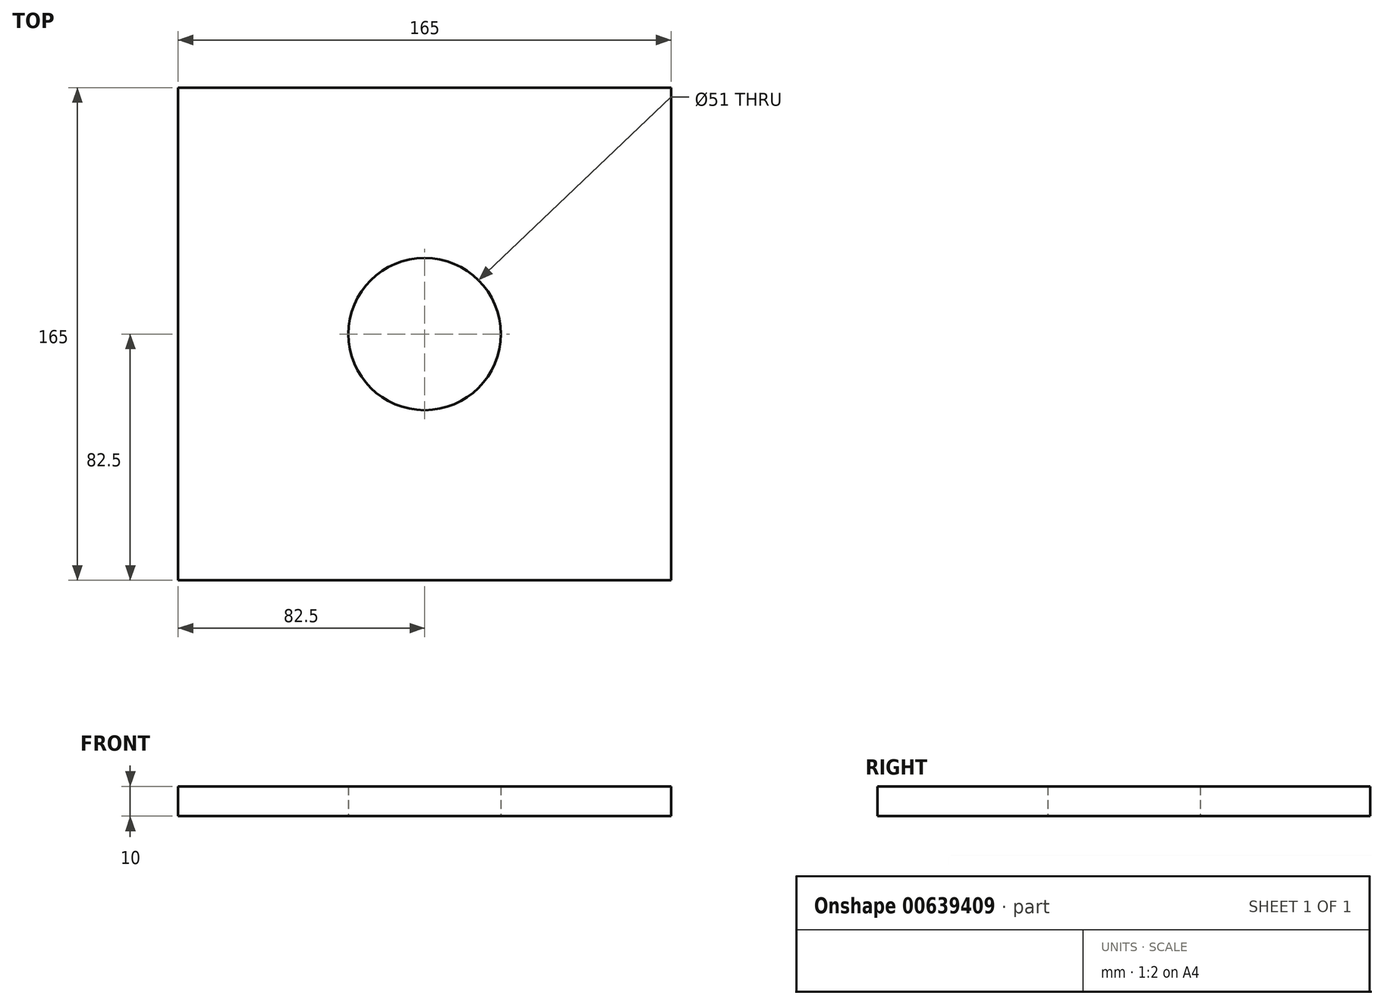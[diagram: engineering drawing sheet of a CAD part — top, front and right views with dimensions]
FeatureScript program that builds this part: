
annotation { "Feature Type Name" : "Feature", "Feature Type Description" : "" }
export const myFeature = defineFeature(function(context is Context, id is Id, definition is map)
    precondition{}
    {
        {
            var Q0;
            Q0=qCreatedBy(makeId("Top.planeOp"),FACE);
            var sketch = newSketch(context, id + "F0", { "sketchPlane" : qUnion([Q0])});
            skLineSegment(sketch, "E0.bottom", {"start": v(0, 0) * mm, "end": v(165, 0) * mm});
            skLineSegment(sketch, "E0.top", {"start": v(0, -165) * mm, "end": v(165, -165) * mm});
            skLineSegment(sketch, "E0.left", {"start": v(0, 0) * mm, "end": v(0, -165) * mm});
            skLineSegment(sketch, "E0.right", {"start": v(165, 0) * mm, "end": v(165, -165) * mm});
            skCircle(sketch, "E1", {"center": v(82.5, -82.5) * mm, "radius": 25.5 * mm});
            skPoint(sketch, "E1.centerSnap0", {"position": v(82.5, 0) * mm});
            skPoint(sketch, "E1.centerSnap1", {"position": v(0, -82.5) * mm});
            skSolve(sketch);
        }
        {
            var Q0;
            Q0=makeQuery(id+"F0.imprint","IMPRINT",FACE,{"disambiguationData":[TD([[makeQuery(id+"F0.imprint","IMPRINT",EDGE,{"derivedFrom":sQuery(id+"F0.wireOp",EDGE,"E0.bottom")}),-1.0]])]});
            extrude(context, id + "F1", {"entities" : qUnion([Q0]), "depth" : 10 * mm, "offsetDistance" : 25 * mm});
        }
    });
